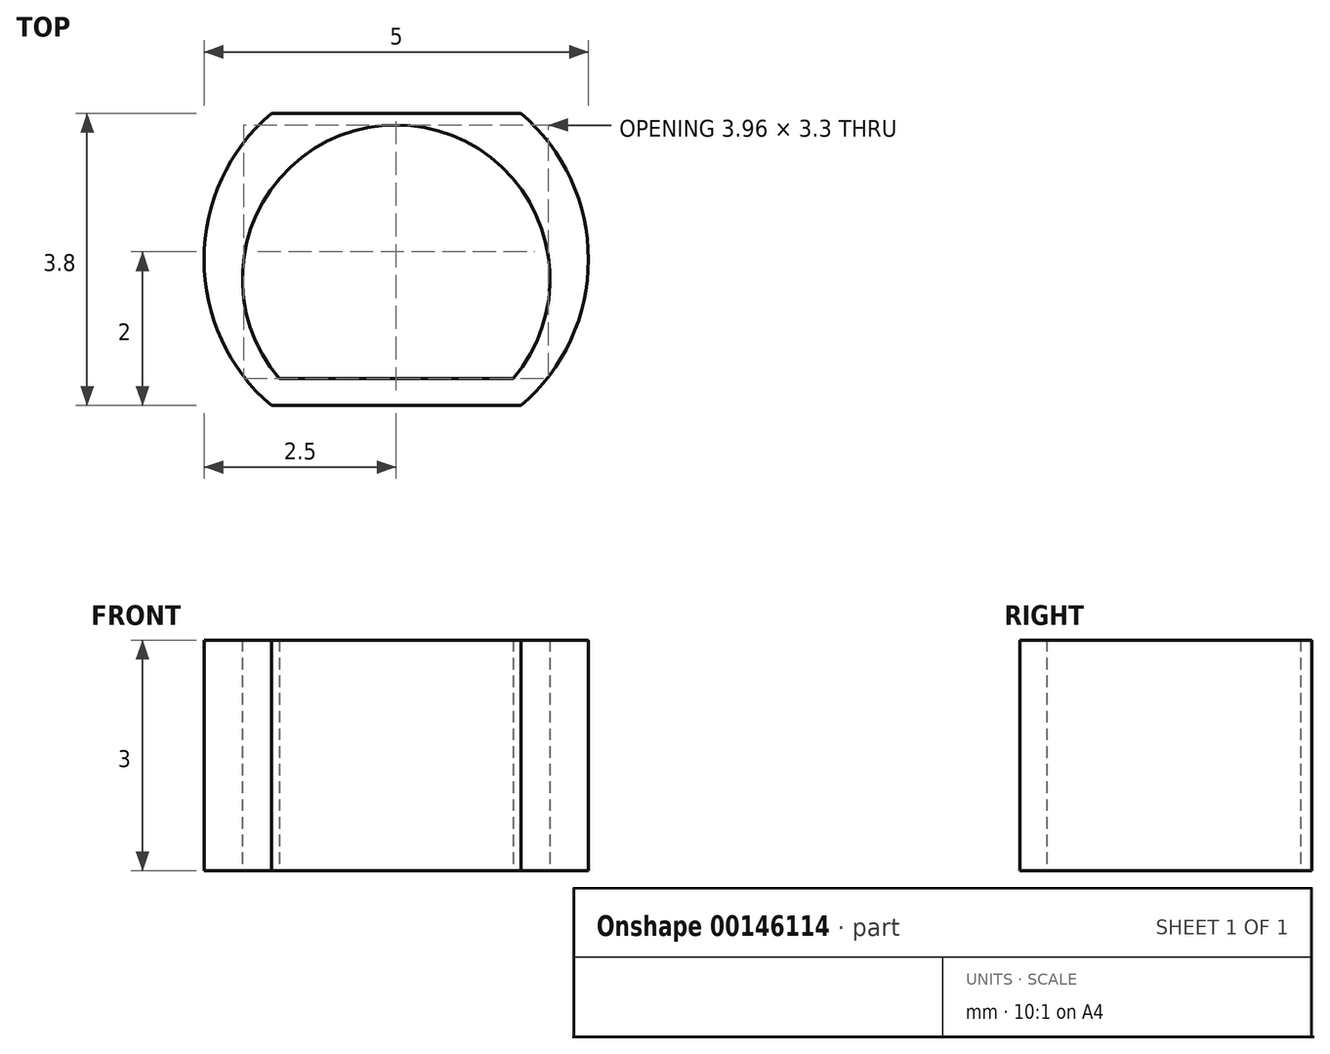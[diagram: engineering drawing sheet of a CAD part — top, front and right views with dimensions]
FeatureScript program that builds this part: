
annotation { "Feature Type Name" : "Feature", "Feature Type Description" : "" }
export const myFeature = defineFeature(function(context is Context, id is Id, definition is map)
    precondition{}
    {
        {
            var Q0;
            Q0=qCreatedBy(makeId("Top.planeOp"),FACE);
            var sketch = newSketch(context, id + "F0", { "sketchPlane" : qUnion([Q0])});
            skLineSegment(sketch, "E0", {"start": v(0, 0) * mm, "end": v(-2.5, 0) * mm, "construction": true});
            skLineSegment(sketch, "E1", {"start": v(-2.5, 0) * mm, "end": v(2.5, 0) * mm, "construction": true});
            skArc(sketch, "E2", {"start": v(1.62, -1.9) * mm, "mid": v(2.5, 0) * mm, "end": v(1.62, 1.9) * mm});
            skLineSegment(sketch, "E3", {"start": v(0, 0) * mm, "end": v(0, 1.9) * mm, "construction": true});
            skLineSegment(sketch, "E4", {"start": v(0, 0) * mm, "end": v(0, -1.9) * mm, "construction": true});
            skLineSegment(sketch, "E5", {"start": v(0, -1.9) * mm, "end": v(1.62, -1.9) * mm});
            skLineSegment(sketch, "E6", {"start": v(1.62, -1.9) * mm, "end": v(-1.62, -1.9) * mm});
            skLineSegment(sketch, "E7", {"start": v(0, 1.9) * mm, "end": v(1.62, 1.9) * mm});
            skLineSegment(sketch, "E8", {"start": v(0, 1.9) * mm, "end": v(-1.62, 1.9) * mm});
            skArc(sketch, "E9.trimOffspring", {"start": v(-1.62, 1.9) * mm, "mid": v(-2.5, 0) * mm, "end": v(-1.62, -1.9) * mm});
            skArc(sketch, "E10", {"start": v(2, -0.13) * mm, "mid": v(2, -0.06) * mm, "end": v(2, 0) * mm});
            skPoint(sketch, "E11", {"position": v(0, 2) * mm});
            skLineSegment(sketch, "E12", {"start": v(0, 2) * mm, "end": v(0, -1.3) * mm, "construction": true});
            skLineSegment(sketch, "E13", {"start": v(0, -1.9) * mm, "end": v(0, -1.55) * mm, "construction": true});
            skPoint(sketch, "E14", {"position": v(0, -1.55) * mm});
            skLineSegment(sketch, "E15", {"start": v(-1.52, -1.55) * mm, "end": v(1.52, -1.55) * mm});
            skLineSegment(sketch, "E16", {"start": v(0, 0) * mm, "end": v(0, -0.25) * mm, "construction": true});
            skArc(sketch, "E17", {"start": v(1.52, -1.55) * mm, "mid": v(0, 1.75) * mm, "end": v(-1.52, -1.55) * mm});
            skArc(sketch, "E18.trimOffspring", {"start": v(-2, 0) * mm, "mid": v(-2, -0.06) * mm, "end": v(-2, -0.12) * mm});
            skSolve(sketch);
        }
        {
            var Q0;
            {var subQ1=sQuery(id+"F0.wireOp",EDGE,"E2");Q0=makeQuery(id+"F0.imprint","IMPRINT",FACE,{"disambiguationData":[TD([[makeQuery(id+"F0.imprint","IMPRINT",EDGE,{"derivedFrom":subQ1}),1.0]])]});}
            extrude(context, id + "F1", {"entities" : qUnion([Q0]), "endBound" : BoundingType.SYMMETRIC, "depth" : 3 * mm});
        }
    });
